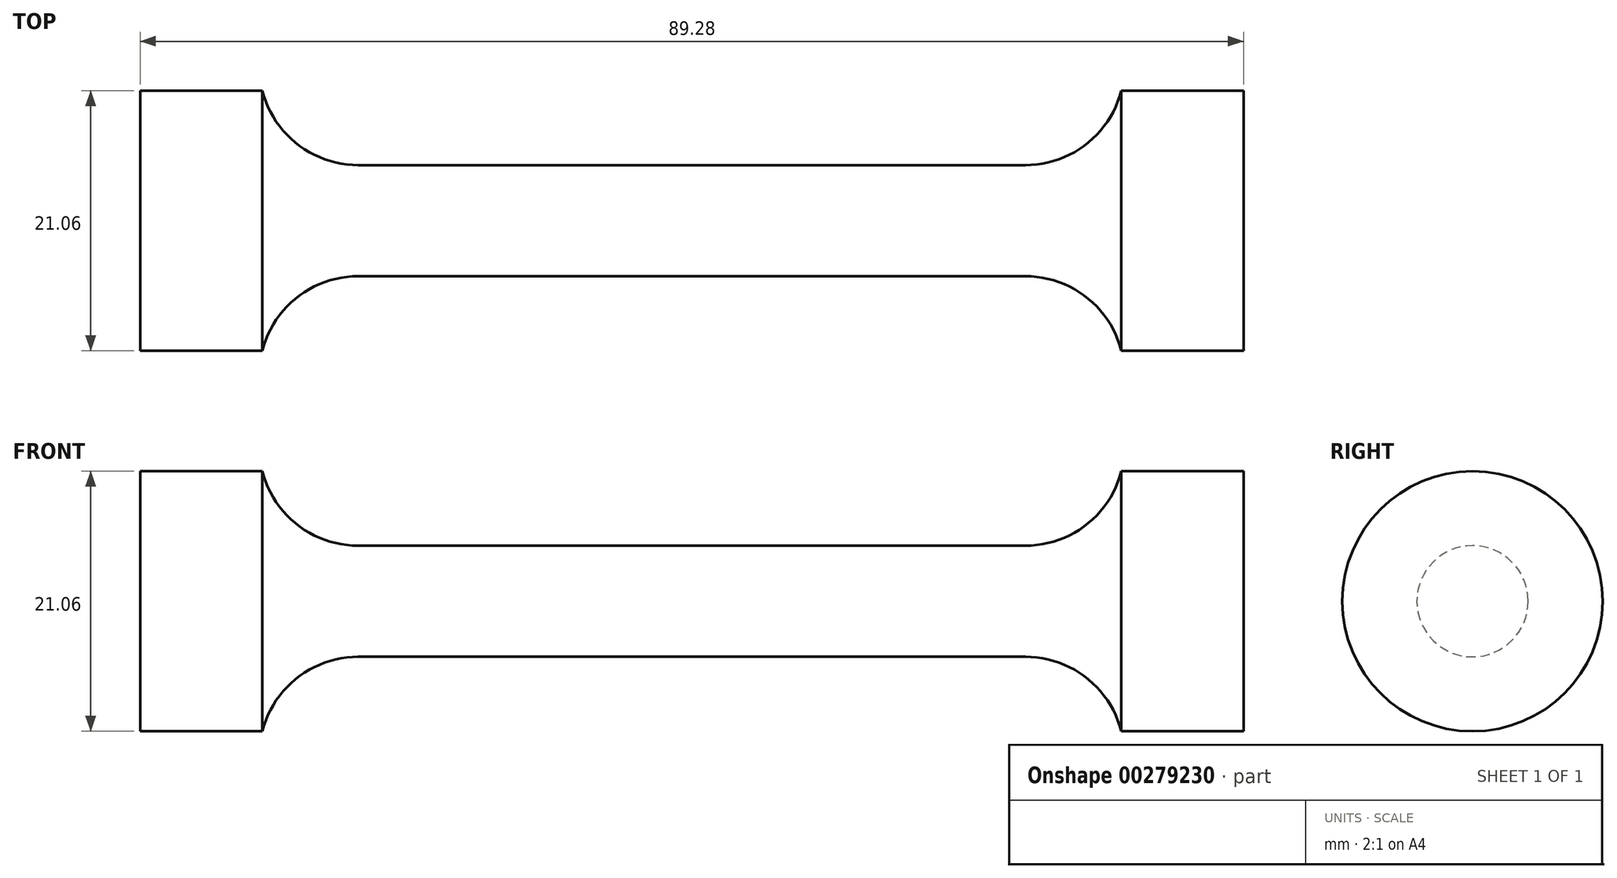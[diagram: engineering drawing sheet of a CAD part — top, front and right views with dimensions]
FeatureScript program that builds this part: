
annotation { "Feature Type Name" : "Feature", "Feature Type Description" : "" }
export const myFeature = defineFeature(function(context is Context, id is Id, definition is map)
    precondition{}
    {
        {
            var Q0;
            Q0=qCreatedBy(makeId("Front.planeOp"),FACE);
            var sketch = newSketch(context, id + "F0", { "sketchPlane" : qUnion([Q0])});
            skLineSegment(sketch, "E0", {"start": v(0, 4.5) * mm, "end": v(27, 4.5) * mm});
            skArc(sketch, "E1", {"start": v(27, 4.5) * mm, "mid": v(31.91, 6.19) * mm, "end": v(34.75, 10.53) * mm});
            skLineSegment(sketch, "E2", {"start": v(34.75, 10.53) * mm, "end": v(44.64, 10.53) * mm});
            skLineSegment(sketch, "E3", {"start": v(44.64, 10.53) * mm, "end": v(44.64, 0) * mm});
            skLineSegment(sketch, "E4.MirrorCS", {"start": v(0, 4.5) * mm, "end": v(-27, 4.5) * mm});
            skLineSegment(sketch, "E5.MirrorCS", {"start": v(-44.64, 10.53) * mm, "end": v(-44.64, 0) * mm});
            skLineSegment(sketch, "E6.MirrorCS", {"start": v(-34.75, 10.53) * mm, "end": v(-44.64, 10.53) * mm});
            skArc(sketch, "E7.MirrorCS", {"start": v(-27, 4.5) * mm, "mid": v(-31.91, 6.19) * mm, "end": v(-34.75, 10.53) * mm});
            skLineSegment(sketch, "E8", {"start": v(-44.64, 0) * mm, "end": v(44.64, 0) * mm});
            skSolve(sketch);
        }
        {
            var Q0;
            Q0=makeQuery(id+"F0.imprint","IMPRINT",FACE,{"disambiguationData":[TD([[makeQuery(id+"F0.imprint","IMPRINT",EDGE,{"derivedFrom":sQuery(id+"F0.wireOp",EDGE,"E0")}),-1.0]])]});
            var Q1;
            Q1=sQuery(id+"F0.wireOp",EDGE,"E8");
            revolve(context, id + "F1", {"entities" : qUnion([Q0]), "axis" : qUnion([Q1]), "revolveType" : RevolveType.FULL});
        }
    });
